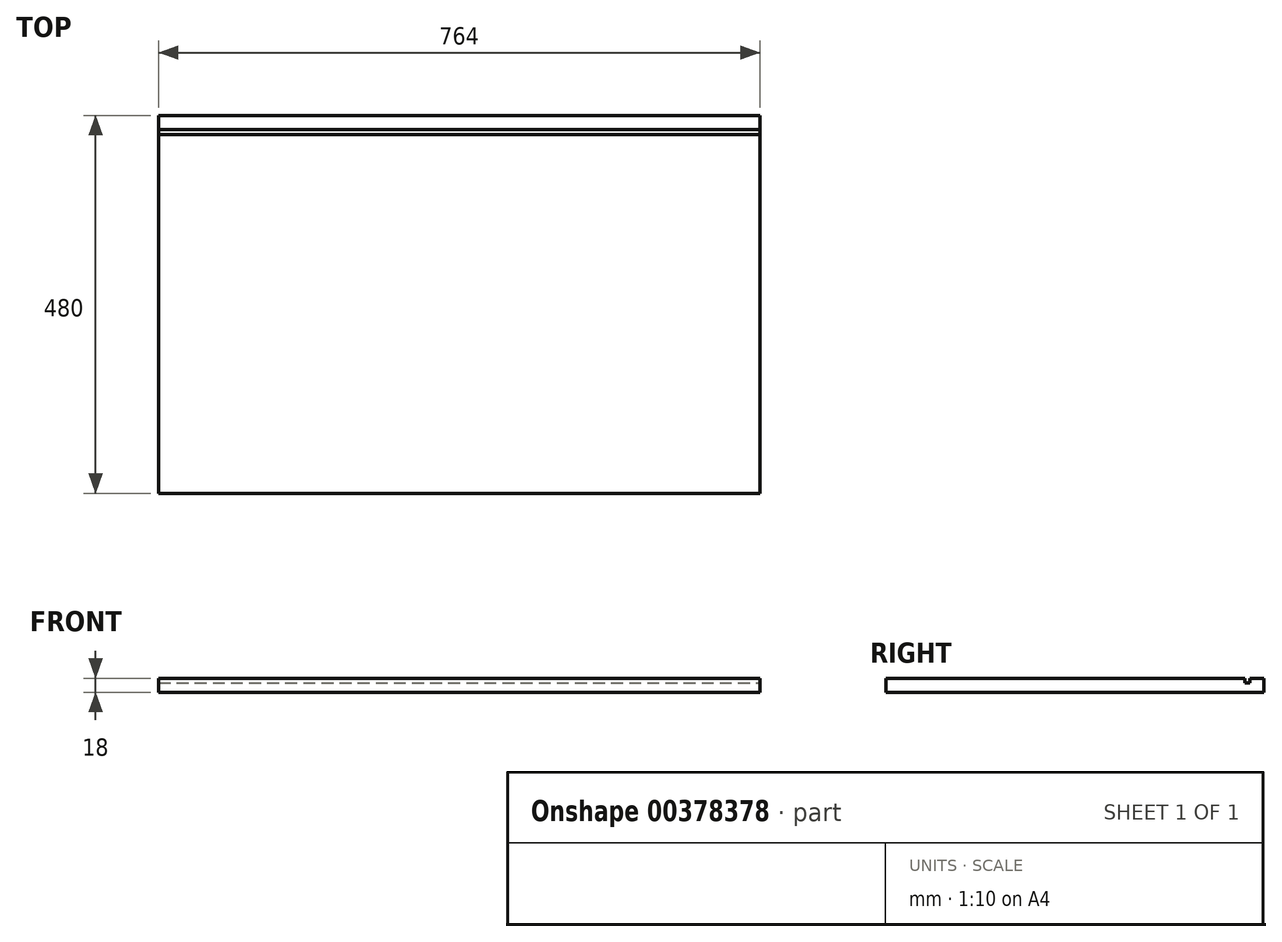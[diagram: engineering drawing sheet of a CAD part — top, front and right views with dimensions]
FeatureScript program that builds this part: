
annotation { "Feature Type Name" : "Feature", "Feature Type Description" : "" }
export const myFeature = defineFeature(function(context is Context, id is Id, definition is map)
    precondition{}
    {
        {
            var Q0;
            Q0=qCreatedBy(makeId("Top.planeOp"),FACE);
            var sketch = newSketch(context, id + "F0", { "sketchPlane" : qUnion([Q0])});
            skLineSegment(sketch, "E0.bottom", {"start": v(382, 240) * mm, "end": v(-382, 240) * mm});
            skLineSegment(sketch, "E0.top", {"start": v(382, -240) * mm, "end": v(-382, -240) * mm});
            skLineSegment(sketch, "E0.right", {"start": v(-382, 240) * mm, "end": v(-382, -240) * mm});
            skPoint(sketch, "E0.middle", {"position": v(0, 0) * mm});
            skLineSegment(sketch, "E1", {"start": v(382, -240) * mm, "end": v(382, 240) * mm});
            skSolve(sketch);
        }
        {
            var Q0;
            Q0=qSketchRegion(id+"F0",true);
            extrude(context, id + "F1", {"entities" : qUnion([Q0]), "depth" : 18 * mm});
        }
        {
            var Q0;
            Q0=makeQuery(id+"F1.opExtrude","CAP_FACE",FACE,{"disambiguationData":[OSD([sQuery(id+"F0.wireOp",EDGE,"E0.bottom"),sQuery(id+"F0.wireOp",EDGE,"E0.top"),sQuery(id+"F0.wireOp",EDGE,"E0.right"),sQuery(id+"F0.wireOp",EDGE,"E1")])],"isStart":false});
            var sketch = newSketch(context, id + "F2", { "sketchPlane" : qUnion([Q0])});
            skLineSegment(sketch, "E2.bottom", {"start": v(-382, 222) * mm, "end": v(382, 222) * mm});
            skLineSegment(sketch, "E2.top", {"start": v(-382, 216) * mm, "end": v(382, 216) * mm});
            skLineSegment(sketch, "E2.left", {"start": v(-382, 222) * mm, "end": v(-382, 216) * mm});
            skLineSegment(sketch, "E2.right", {"start": v(382, 222) * mm, "end": v(382, 216) * mm});
            skSolve(sketch);
        }
        {
            var Q0;
            Q0=qSketchRegion(id+"F2",true);
            extrude(context, id + "F3", {"entities" : qUnion([Q0]), "operationType" : NewBodyOperationType.REMOVE, "oppositeDirection" : true, "depth" : 6 * mm});
        }
    });
